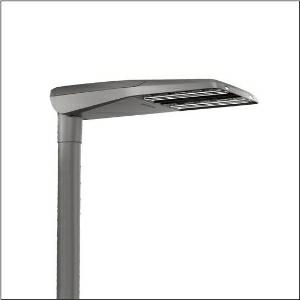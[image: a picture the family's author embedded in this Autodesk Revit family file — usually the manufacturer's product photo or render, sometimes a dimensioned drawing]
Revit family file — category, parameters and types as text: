
# Revit family: streetlight_sl_11_iq_midi___st1_2a_5xc3a11f08me_159a
name_source: partatom
category: Lighting Fixtures
units: mm (PartAtom-declared; Revit-internal decimal feet)

## family parameters
Cut with Voids When Loaded = No
Host = Face
Light Source = No
Part Type = Normal
Room Calculation Point = No
Round Connector Dimension = Use Diameter
Shared = No

## types (1)
- --- (1 x LED, 11170 lm, 124.5 W, 1800K)
    Apparent Load = 125 VA
    CIE Flux Codes = 32 70 96 100 100
    Color Rendering = 70
    Color Temperature = 1800K
    Default Elevation = 1800 mm  [stored 5.90551 ft]
    Description = Streetlight SL 11 iQ midi, mast luminaire, primary light control with 3 zone facetted reflector, of plastic, silver coated, highly specular, primary optical cover: cover, of PMMA, transparent, light distribution: ST1.2a, light emission: direct distribution, primary light characteristic: asymmetric, installation type: post-top, side-entry, lamps: LED, High Power LED, rated values: 11.170lm | 124,5W | 89,7lm/W (begin service life); end service life: 11.170lm | 131,6W; at 50% lumin. flux: 5.585lm | 55,1W | 101,4lm/W, colour temperature: 1800K, colour rendering: CRI > 70, light colour: 718, light setting 1 begin service life: 100% | 11.170lm | 124,5W | 89,7lm/W | 1.800K, light setting 1 end service life: 131,6W, further light settings possible, control: Street-Remote, Auto-Match, Temp-Guard, Lumen-Switch, Night-Set, Smart-Wire, Light-Fading, Desk-Remote (wireless, voltage-free reading and setting of iQ features in the workshop via application-optimized NFC function/RFID function), optimised constant luminous flux control (CLO 2.0), with cable H07RN-F 3x 1.5mm², mains connection: 230..240V, AC, 50/60Hz, connection cable pre-assembled, cable length: 12,5m, luminaire housing, of diecast aluminium, powder-coated, SITECO metallic grey (DB 702S), please order mast flange separately, inclination adjustable without tools: 0°, 5°, 10°, 15° (post-top) | 0°, -5°, -10°, -15° (side-entry), sealing non-destructively replaceable, multi-level sealing system, length: 780mm, width: 376mm, height: 118mm, mast flange for spigot size: 42mm (side-entry): 5XC10008XM4, 60/48mm (side-entry/post-top): 5XC10108XM2, 76/60mm (side-entry/post-top): 5XC10108XM1, equipment: Power, protection rating (complete): IP66, insulation class (complete): insulation class II (safety insulation), certification: CE, ENEC, ENEC+, VDE, impact resistance: IK10, permissible operating ambient temperature for outdoor applications: -25..+50°C, standard-compliant lighting for roads and squares, Environmental Product Declaration (EPD) tested and certified by an independent institute, packaging unit: 1 piece

Light Distribution: ST1.2a
    Height = 118 mm
    Lamp = 1 x LED
    Lamp Light Flux = 11170 lm
    Lamp Power = 124.5 W
    Lamp count = 1
    Length = 780 mm
    Luminous efficacy = 90 lm/W
    Manufacturer = Siteco
    ModVariant = No
    Model = 5XC3A11F08ME
    Number of Poles = 1
    OnlyDefault = Yes
    Power Factor = 1
    Product Name = Streetlight SL 11 iQ midi | ST1.2a
    Product group = mast luminaire | pylon top
    ProductGroupID = 6100
    Protection Class = Protection class II
    Protection Degree = IP 66
    RLX_Detail_Level = 1
    RLX_Emergency_Light_Flux = 0 lm
    RLX_Emergency_Type = 0
    RLX_Emergency_Type_DB = No
    RlxData = <blob elided: 70901 chars, md5=e616a788>
    Socket = socket
    Standby Power = 0 W
    System Light Flux = 11170 lm
    System Power = 125 W
    Type Comments = factory setting: luminous flux: 100 % | dim-lin: 254 | 554 mA
    Type Image = l_1005960.jpg
    URL = http://relux.com
    VarID = @adj_086111
    Voltage = 0 V
    Weight = 0.00 kg
    Width = 376 mm

note: [stored X ft] marks values corroborated as IEEE doubles in the binary element streams (Revit-internal decimal feet)

## geometry (parser evidence)
native form markers: Blend x4, Sweep x12
no freeform markers — native parametric forms only
